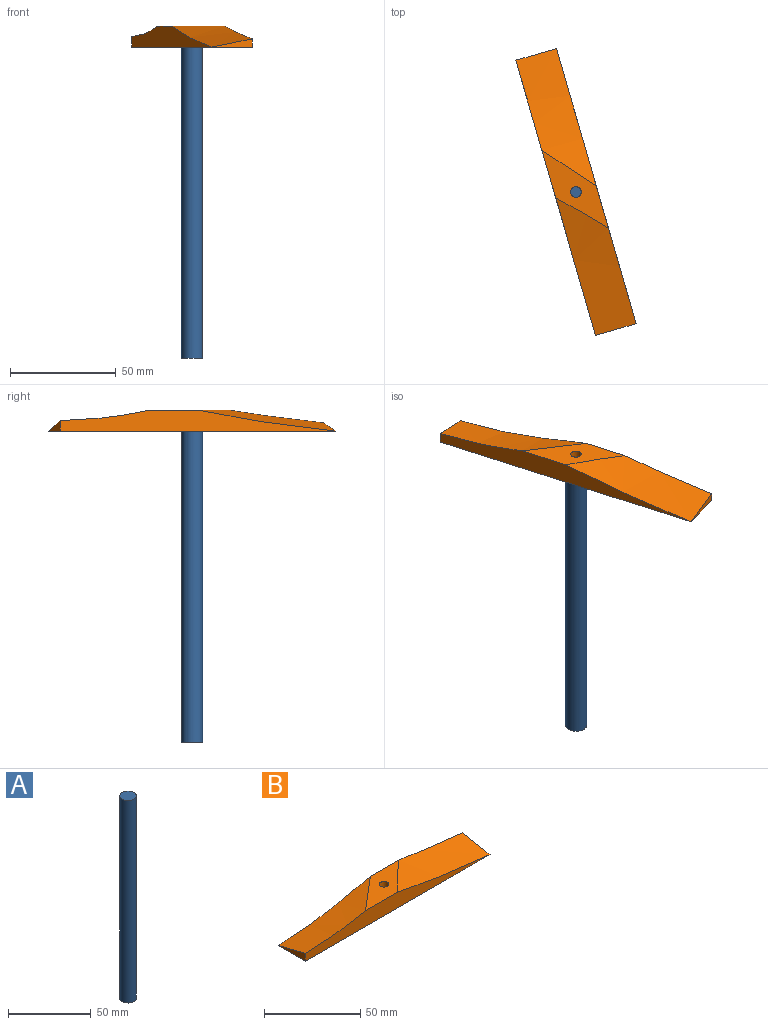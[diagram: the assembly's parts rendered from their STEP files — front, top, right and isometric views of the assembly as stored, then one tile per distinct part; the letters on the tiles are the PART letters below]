
ASSEMBLY  parts=2 mates=1
PART A: 3 faces, bbox 10x10x150 mm
  f0: cylinder r=5mm len=150mm, axis (0,0,-1), area 4712.4mm2, adj f1,f2
  f1: plane 10x10mm, normal (0,0,1), area 78.5mm2, adj f0
  f2: plane 10x10mm, normal (0,0,-1), area 78.5mm2, adj f0
PART B: 11 faces, bbox 135.5x20x15 mm
  f0: plane 135.46x10.19mm, normal (0,-1,0), area 834.5mm2, adj f3,f4,f5,f6,f7
  f1: plane 20x3.91mm, normal (1,0,0), area 39.1mm2, adj f2,f5,f6
  f2: plane 135.46x10.2mm, normal (0,1,0), area 778.8mm2, adj f1,f4,f5,f6,f7
  f3: plane 20x5mm, normal (-1,0,0), area 50mm2, adj f0,f5,f7
  f4: plane 44.28x20mm, normal (0,0,1), area 413.8mm2, adj f0,f2,f6,f7,f8
  f5: plane 135.46x20mm, normal (0,0,-1), area 2630.6mm2, adj f0,f1,f2,f3,f10
  f6: bspline ~67.73x20mm, area 1185.5mm2, adj f0,f1,f2,f4
  f7: bspline ~67.73x20mm, area 1169.6mm2, adj f0,f2,f3,f4
  f8: cylinder r=2.5mm len=7mm, axis (0,0,-1), area 110mm2, adj f4,f9
  f9: plane 10x10mm, normal (0,0,-1), area 58.9mm2, adj f8,f10
  f10: cylinder r=5mm len=10mm, axis (0,0,-1), area 94.2mm2, adj f5,f9
PLACE A t=(-40.81,16.98,-14.19)mm fixed
PLACE B rot(axis=(0,0,-1),73.8deg) t=(-40.8,17,137.81)mm
MATE revolute A.f0 <-> B.f8  axis (0,0,1) through (-40.81,16.98,135.81)mm
